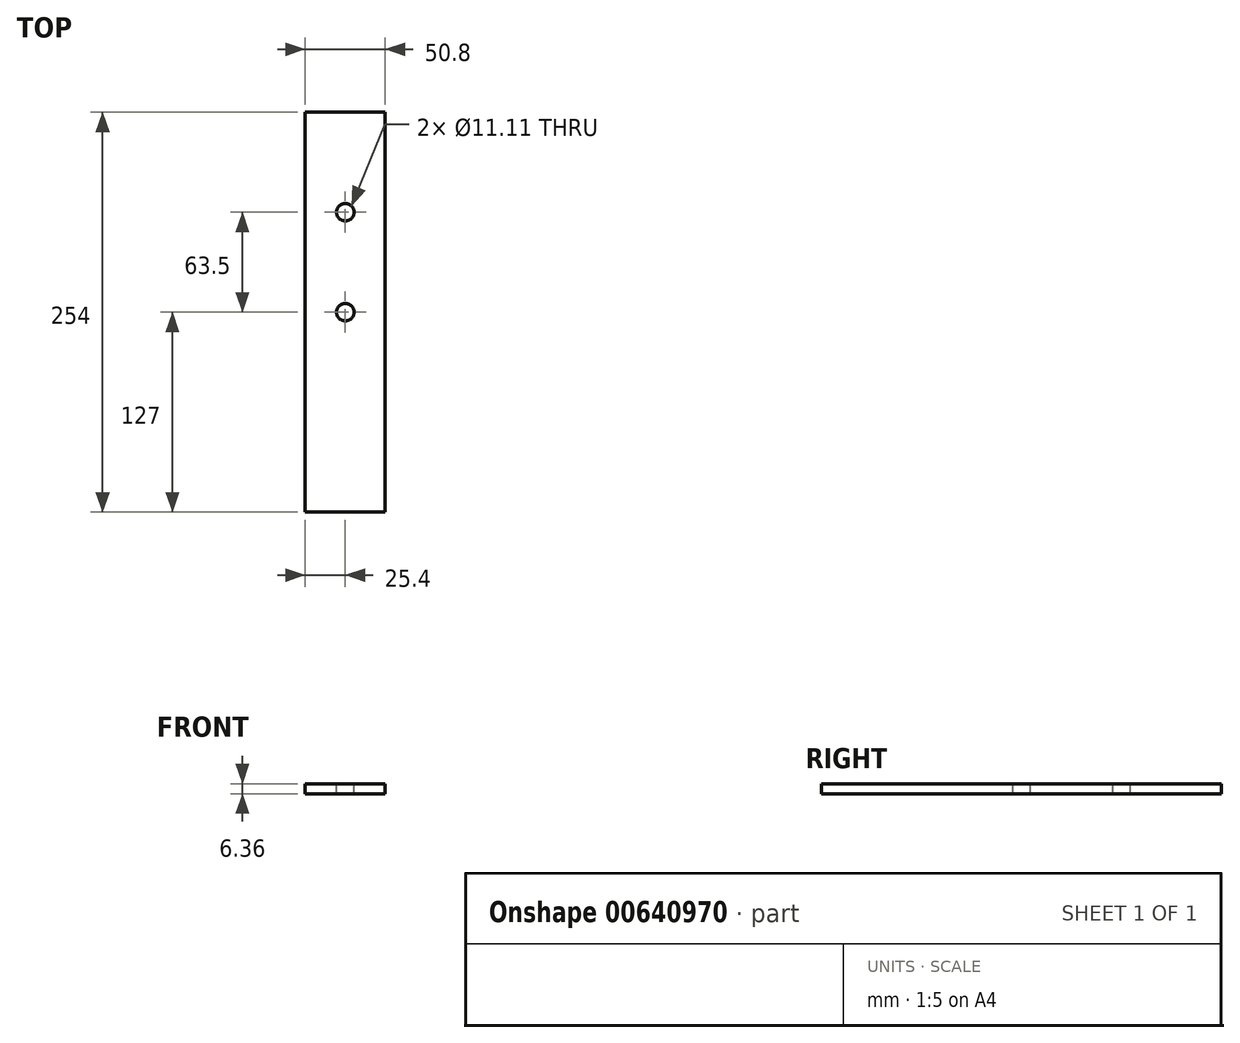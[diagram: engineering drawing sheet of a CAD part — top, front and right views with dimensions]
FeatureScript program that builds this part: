
annotation { "Feature Type Name" : "Feature", "Feature Type Description" : "" }
export const myFeature = defineFeature(function(context is Context, id is Id, definition is map)
    precondition{}
    {
        {
            var Q0;
            Q0=qCreatedBy(makeId("Front.planeOp"),FACE);
            var sketch = newSketch(context, id + "F0", { "sketchPlane" : qUnion([Q0])});
            skLineSegment(sketch, "E0.bottom", {"start": v(-25.4, 3.18) * mm, "end": v(25.4, 3.18) * mm});
            skLineSegment(sketch, "E0.top", {"start": v(-25.4, -3.18) * mm, "end": v(25.4, -3.18) * mm});
            skLineSegment(sketch, "E0.left", {"start": v(-25.4, 3.18) * mm, "end": v(-25.4, -3.18) * mm});
            skLineSegment(sketch, "E0.right", {"start": v(25.4, 3.17) * mm, "end": v(25.4, -3.18) * mm});
            skSolve(sketch);
        }
        {
            var Q0;
            Q0 = qSketchRegion(id + "F0", true);
            extrude(context, id + "F1", {"entities" : qUnion([Q0]), "endBound" : BoundingType.SYMMETRIC, "depth" : 254 * mm, "offsetDistance" : 25.4 * mm});
        }
        {
            var Q0;
            Q0=makeQuery(id+"F1.opExtrude","SWEPT_FACE",FACE,{"disambiguationData":[OSD([sQuery(id+"F0.wireOp",EDGE,"E0.bottom")])]});
            var sketch = newSketch(context, id + "F2", { "sketchPlane" : qUnion([Q0])});
            skCircle(sketch, "E1", {"center": v(0, 63.5) * mm, "radius": 5.56 * mm});
            skCircle(sketch, "E2", {"center": v(0, 0) * mm, "radius": 5.56 * mm});
            skSolve(sketch);
        }
        {
            var Q0;
            Q0=makeQuery(id+"F2.imprint","IMPRINT",FACE,{"disambiguationData":[TD([[makeQuery(id+"F2.imprint","IMPRINT",EDGE,{"derivedFrom":sQuery(id+"F2.wireOp",EDGE,"E1")}),1.0]])]});
            var Q1;
            Q1=makeQuery(id+"F2.imprint","IMPRINT",FACE,{"disambiguationData":[TD([[makeQuery(id+"F2.imprint","IMPRINT",EDGE,{"derivedFrom":sQuery(id+"F2.wireOp",EDGE,"E2")}),1.0]])]});
            extrude(context, id + "F3", {"entities" : qUnion([Q0, Q1]), "operationType" : NewBodyOperationType.REMOVE, "endBound" : BoundingType.THROUGH_ALL, "oppositeDirection" : true, "depth" : 25.4 * mm, "offsetDistance" : 25.4 * mm});
        }
    });
